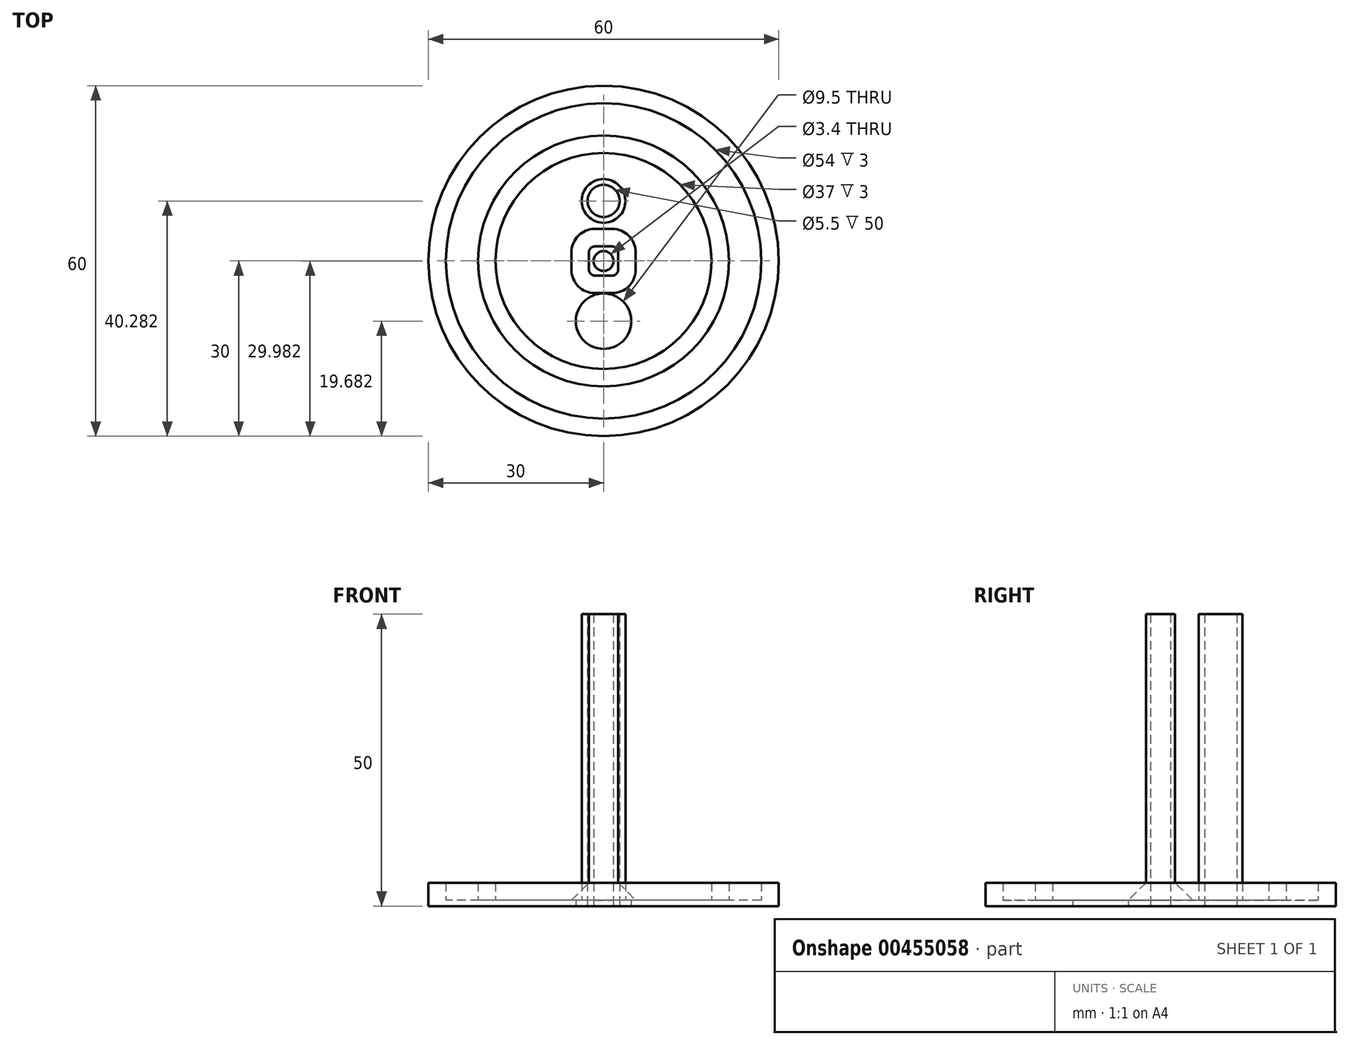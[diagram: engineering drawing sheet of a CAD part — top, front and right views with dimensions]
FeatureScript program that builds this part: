
annotation { "Feature Type Name" : "Feature", "Feature Type Description" : "" }
export const myFeature = defineFeature(function(context is Context, id is Id, definition is map)
    precondition{}
    {
        {
            var Q0;
            Q0=qCreatedBy(makeId("Top.planeOp"),FACE);
            var sketch = newSketch(context, id + "F0", { "sketchPlane" : qUnion([Q0])});
            skCircle(sketch, "E0", {"center": v(0, 0) * mm, "radius": 27 * mm});
            skCircle(sketch, "E1", {"center": v(0, 0) * mm, "radius": 30 * mm});
            skCircle(sketch, "E2", {"center": v(0, 0) * mm, "radius": 21.5 * mm});
            skCircle(sketch, "E3", {"center": v(0, 10.28) * mm, "radius": 3.75 * mm});
            skCircle(sketch, "E4", {"center": v(0, -10.32) * mm, "radius": 4.75 * mm});
            skCircle(sketch, "E5", {"center": v(0, 0) * mm, "radius": 18.5 * mm});
            skCircle(sketch, "E6", {"center": v(0, -0.02) * mm, "radius": 1.7 * mm});
            skLineSegment(sketch, "E7.bottom", {"start": v(2.5, -2.52) * mm, "end": v(-2.5, -2.52) * mm});
            skLineSegment(sketch, "E7.top", {"start": v(2.5, 2.48) * mm, "end": v(-2.5, 2.48) * mm});
            skLineSegment(sketch, "E7.left", {"start": v(2.5, -2.52) * mm, "end": v(2.5, 2.48) * mm});
            skLineSegment(sketch, "E7.right", {"start": v(-2.5, -2.52) * mm, "end": v(-2.5, 2.48) * mm});
            skCircle(sketch, "E8", {"center": v(0.36, 0) * mm, "radius": 17.56 * mm, "construction": true});
            skCircle(sketch, "E9", {"center": v(0, 10.28) * mm, "radius": 2.75 * mm});
            skSolve(sketch);
        }
        {
            var Q0;
            Q0=makeQuery(id+"F0.imprint","IMPRINT",FACE,{"disambiguationData":[TD([[makeQuery(id+"F0.imprint","IMPRINT",EDGE,{"derivedFrom":sQuery(id+"F0.wireOp",EDGE,"E4")}),-1.0]])]});
            var Q1;
            Q1=makeQuery(id+"F0.imprint","IMPRINT",FACE,{"disambiguationData":[TD([[makeQuery(id+"F0.imprint","IMPRINT",EDGE,{"derivedFrom":sQuery(id+"F0.wireOp",EDGE,"E6")}),-1.0]])]});
            var Q2;
            Q2=makeQuery(id+"F0.imprint","IMPRINT",FACE,{"disambiguationData":[TD([[makeQuery(id+"F0.imprint","IMPRINT",EDGE,{"derivedFrom":sQuery(id+"F0.wireOp",EDGE,"E5")}),-1.0]])]});
            var Q3;
            Q3=makeQuery(id+"F0.imprint","IMPRINT",FACE,{"disambiguationData":[TD([[makeQuery(id+"F0.imprint","IMPRINT",EDGE,{"derivedFrom":sQuery(id+"F0.wireOp",EDGE,"E0")}),1.0]])]});
            var Q4;
            Q4=makeQuery(id+"F0.imprint","IMPRINT",FACE,{"disambiguationData":[TD([[makeQuery(id+"F0.imprint","IMPRINT",EDGE,{"derivedFrom":sQuery(id+"F0.wireOp",EDGE,"E0")}),-1.0]])]});
            extrude(context, id + "F1", {"entities" : qUnion([Q0, Q1, Q2, Q3, Q4]), "depth" : 1 * mm});
        }
        {
            var Q0;
            Q0=makeQuery(id+"F0.imprint","IMPRINT",FACE,{"disambiguationData":[TD([[makeQuery(id+"F0.imprint","IMPRINT",EDGE,{"derivedFrom":sQuery(id+"F0.wireOp",EDGE,"E0")}),-1.0]])]});
            var Q1;
            Q1=makeQuery(id+"F0.imprint","IMPRINT",FACE,{"disambiguationData":[TD([[makeQuery(id+"F0.imprint","IMPRINT",EDGE,{"derivedFrom":sQuery(id+"F0.wireOp",EDGE,"E5")}),-1.0]])]});
            extrude(context, id + "F2", {"entities" : qUnion([Q0, Q1]), "operationType" : NewBodyOperationType.ADD, "depth" : 4 * mm});
        }
        {
            var Q0;
            Q0=makeQuery(id+"F0.imprint","IMPRINT",FACE,{"disambiguationData":[TD([[makeQuery(id+"F0.imprint","IMPRINT",EDGE,{"derivedFrom":sQuery(id+"F0.wireOp",EDGE,"E6")}),-1.0]])]});
            var Q1;
            Q1=makeQuery(id+"F0.imprint","IMPRINT",FACE,{"disambiguationData":[TD([[makeQuery(id+"F0.imprint","IMPRINT",EDGE,{"derivedFrom":sQuery(id+"F0.wireOp",EDGE,"E3")}),1.0]])]});
            extrude(context, id + "F3", {"entities" : qUnion([Q0, Q1]), "operationType" : NewBodyOperationType.ADD, "depth" : 50 * mm});
        }
        {
            var Q0;
            Q0=makeQuery(id+"F3.opExtrude","SWEPT_EDGE",EDGE,{"disambiguationData":[OSD([sQuery(id+"F0.wireOp",EDGE,"E7.bottom"),sQuery(id+"F0.wireOp",EDGE,"E7.right")])]});
            var Q1;
            Q1=makeQuery(id+"F3.opExtrude","SWEPT_EDGE",EDGE,{"disambiguationData":[OSD([sQuery(id+"F0.wireOp",EDGE,"E7.bottom"),sQuery(id+"F0.wireOp",EDGE,"E7.left")])]});
            var Q2;
            Q2=makeQuery(id+"F3.opExtrude","SWEPT_EDGE",EDGE,{"disambiguationData":[OSD([sQuery(id+"F0.wireOp",EDGE,"E7.top"),sQuery(id+"F0.wireOp",EDGE,"E7.right")])]});
            var Q3;
            Q3=makeQuery(id+"F3.opExtrude","SWEPT_EDGE",EDGE,{"disambiguationData":[OSD([sQuery(id+"F0.wireOp",EDGE,"E7.top"),sQuery(id+"F0.wireOp",EDGE,"E7.left")])]});
            fillet(context, id + "F4", {"entities" : qUnion([Q0, Q1, Q2, Q3]), "radius" : 1 * mm, "tangentPropagation" : true, "allowEdgeOverflow" : false});
        }
        {
            var Q0;
            {var subQ0=sQuery(id+"F0.wireOp",EDGE,"E4");var subQ1=sQuery(id+"F0.wireOp",EDGE,"E6");Q0=makeQuery(id+"F3.boolean.opBoolean","INTERSECT",EDGE,{"derivedFrom":[makeQuery(id+"F2.boolean.opBoolean","SPLIT",FACE,{"disambiguationData":[TD([makeQuery(id+"F1.opExtrude","SWEPT_FACE",FACE,{"disambiguationData":[OSD([subQ0])]})])],"derivedFrom":makeQuery(id+"F1.opExtrude","CAP_FACE",FACE,{"disambiguationData":[OSD([sQuery(id+"F0.wireOp",EDGE,"E1"),sQuery(id+"F0.wireOp",EDGE,"E3"),subQ0,subQ1])],"isStart":false})}),makeQuery(id+"F3.opExtrude","SWEPT_FACE",FACE,{"disambiguationData":[OSD([sQuery(id+"F0.wireOp",EDGE,"E7.bottom")])]})]});}
            var Q1;
            {var subQ0=sQuery(id+"F0.wireOp",EDGE,"E4");var subQ1=sQuery(id+"F0.wireOp",EDGE,"E6");Q1=makeQuery(id+"F4.opFillet","BLEND_EDGE",EDGE,{"blendedFrom":[makeQuery(id+"F3.opExtrude","SWEPT_EDGE",EDGE,{"disambiguationData":[OSD([sQuery(id+"F0.wireOp",EDGE,"E7.bottom"),sQuery(id+"F0.wireOp",EDGE,"E7.right")])]}),makeQuery(id+"F2.boolean.opBoolean","SPLIT",FACE,{"disambiguationData":[TD([makeQuery(id+"F1.opExtrude","SWEPT_FACE",FACE,{"disambiguationData":[OSD([subQ0])]})])],"derivedFrom":makeQuery(id+"F1.opExtrude","CAP_FACE",FACE,{"disambiguationData":[OSD([sQuery(id+"F0.wireOp",EDGE,"E1"),sQuery(id+"F0.wireOp",EDGE,"E3"),subQ0,subQ1])],"isStart":false})})],"blendedInto":[makeQuery(id+"F2.boolean.opBoolean","SPLIT",FACE,{"disambiguationData":[TD([makeQuery(id+"F1.opExtrude","SWEPT_FACE",FACE,{"disambiguationData":[OSD([subQ0])]})])],"derivedFrom":makeQuery(id+"F1.opExtrude","CAP_FACE",FACE,{"disambiguationData":[OSD([sQuery(id+"F0.wireOp",EDGE,"E1"),sQuery(id+"F0.wireOp",EDGE,"E3"),subQ0,subQ1])],"isStart":false})})]});}
            var Q2;
            Q2=makeQuery(id+"F1.opExtrude","CAP_EDGE",EDGE,{"disambiguationData":[OSD([sQuery(id+"F0.wireOp",EDGE,"E3")])],"isStart":false});
            chamfer(context, id + "F5", {"entities" : qUnion([Q0, Q1, Q2]), "width" : 3 * mm, "tangentPropagation" : true});
        }
    });
